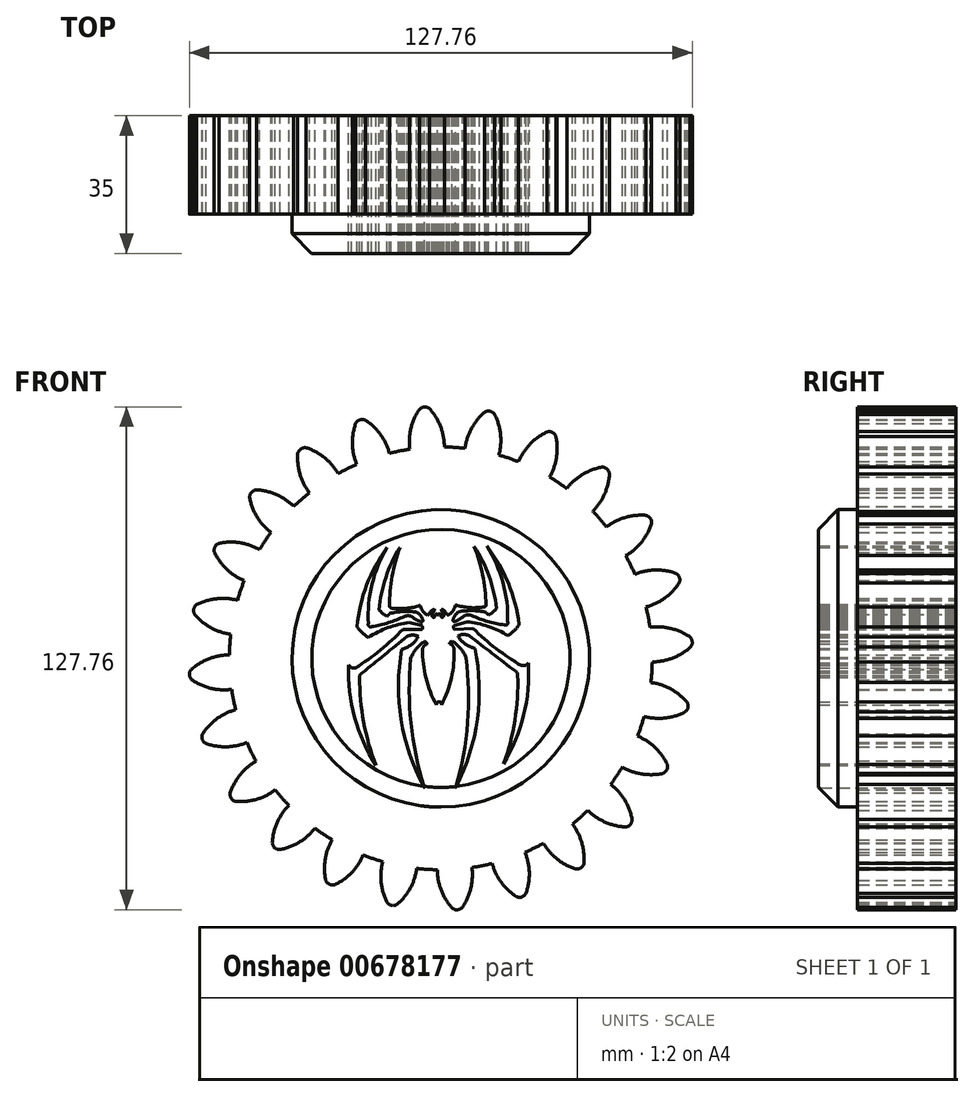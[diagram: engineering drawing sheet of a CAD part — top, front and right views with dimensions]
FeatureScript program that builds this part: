
annotation { "Feature Type Name" : "Feature", "Feature Type Description" : "" }
export const myFeature = defineFeature(function(context is Context, id is Id, definition is map)
    precondition{}
    {
        {
            var Q0;
            Q0=qCreatedBy(makeId("Front.planeOp"),FACE);
            var sketch = newSketch(context, id + "F0", { "sketchPlane" : qUnion([Q0])});
            skCircle(sketch, "E0", {"center": v(0, 0) * mm, "radius": 53.72 * mm});
            skCircle(sketch, "E1", {"center": v(0, 0) * mm, "radius": 58.67 * mm, "construction": true});
            skCircle(sketch, "E2", {"center": v(0, 0) * mm, "radius": 63.5 * mm, "construction": true});
            skLineSegment(sketch, "E3", {"start": v(0, 0) * mm, "end": v(0, 78.32) * mm, "construction": true});
            skLineSegment(sketch, "E4", {"start": v(0, 0) * mm, "end": v(-7.18, 109.5) * mm, "construction": true});
            skLineSegment(sketch, "E5", {"start": v(0, 58.67) * mm, "end": v(-85.63, 58.67) * mm, "construction": true});
            skLineSegment(sketch, "E6", {"start": v(0, 58.67) * mm, "end": v(-86.28, 27.27) * mm, "construction": true});
            skCircle(sketch, "E7", {"center": v(0, 0) * mm, "radius": 55.14 * mm, "construction": true});
            skCircle(sketch, "E8", {"center": v(0, 58.67) * mm, "radius": 14.6 * mm, "construction": true});
            skCircle(sketch, "E9", {"center": v(-13.72, 53.68) * mm, "radius": 14.6 * mm, "construction": true});
            skArc(sketch, "E10", {"start": v(0, 58.67) * mm, "mid": v(-1.2, 61.19) * mm, "end": v(-2.86, 63.44) * mm});
            skArc(sketch, "E11", {"start": v(0.88, 53.71) * mm, "mid": v(0.66, 56.23) * mm, "end": v(0, 58.67) * mm});
            skArc(sketch, "E12.MirrorCS", {"start": v(-7.88, 53.14) * mm, "mid": v(-8, 55.67) * mm, "end": v(-7.66, 58.17) * mm});
            skArc(sketch, "E13.MirrorCS", {"start": v(-7.66, 58.17) * mm, "mid": v(-6.8, 60.82) * mm, "end": v(-5.45, 63.27) * mm});
            skArc(sketch, "E14", {"start": v(-2.86, 63.44) * mm, "mid": v(-4.19, 63.88) * mm, "end": v(-5.45, 63.27) * mm});
            skArc(sketch, "E15", {"start": v(-13.64, 28.2) * mm, "mid": v(-18.83, 18.65) * mm, "end": v(-21.3, 8.08) * mm});
            skArc(sketch, "E16", {"start": v(-8.04, 9.1) * mm, "mid": v(-13.45, 7.8) * mm, "end": v(-18.43, 5.32) * mm});
            skLineSegment(sketch, "E17", {"start": v(-8.04, 9.1) * mm, "end": v(-4.86, 8.31) * mm});
            skLineSegment(sketch, "E18", {"start": v(-4.86, 7.29) * mm, "end": v(-9.63, 7.36) * mm});
            skLineSegment(sketch, "E19", {"start": v(-21.65, -2.4) * mm, "end": v(-22.74, -2.4) * mm});
            skLineSegment(sketch, "E20", {"start": v(-22.74, -2.4) * mm, "end": v(-23.41, -1.69) * mm});
            skArc(sketch, "E21", {"start": v(-23.41, -1.69) * mm, "mid": v(-21.9, -14.97) * mm, "end": v(-16.5, -27.2) * mm});
            skArc(sketch, "E22", {"start": v(-20.63, -4.83) * mm, "mid": v(-19.61, -16.2) * mm, "end": v(-16.5, -27.2) * mm});
            skArc(sketch, "E23", {"start": v(-9.94, 2.28) * mm, "mid": v(-7.48, 3.5) * mm, "end": v(-5.7, 5.59) * mm});
            skArc(sketch, "E24", {"start": v(-9.94, 2.28) * mm, "mid": v(-10.07, -15.84) * mm, "end": v(-4.14, -32.97) * mm});
            skArc(sketch, "E25", {"start": v(-7.65, 0) * mm, "mid": v(-7.58, -16.66) * mm, "end": v(-4.14, -32.97) * mm});
            skArc(sketch, "E26", {"start": v(-4.14, 4.28) * mm, "mid": v(-6.25, 2.43) * mm, "end": v(-7.65, 0) * mm});
            skArc(sketch, "E27", {"start": v(-3.56, 3.63) * mm, "mid": v(-3.72, 4.07) * mm, "end": v(-4.14, 4.28) * mm});
            skArc(sketch, "E28", {"start": v(-3.56, 3.63) * mm, "mid": v(-4.29, 3.1) * mm, "end": v(-4.65, 2.28) * mm});
            skArc(sketch, "E29", {"start": v(-4.65, 2.28) * mm, "mid": v(-3.78, -5) * mm, "end": v(-1.1, -11.85) * mm});
            skArc(sketch, "E30", {"start": v(-0.45, -11.09) * mm, "mid": v(-1, -11.27) * mm, "end": v(-1.1, -11.85) * mm});
            skArc(sketch, "E31", {"start": v(-4.86, 7.29) * mm, "mid": v(-4.65, 7.8) * mm, "end": v(-4.86, 8.31) * mm});
            skArc(sketch, "E32", {"start": v(-21.65, -2.4) * mm, "mid": v(-15.34, 2.11) * mm, "end": v(-9.63, 7.36) * mm});
            skArc(sketch, "E33", {"start": v(-5.7, 5.59) * mm, "mid": v(-7.13, 5.9) * mm, "end": v(-8.56, 5.59) * mm});
            skArc(sketch, "E34", {"start": v(-20.05, -3.75) * mm, "mid": v(-14.3, 0.92) * mm, "end": v(-8.56, 5.59) * mm});
            skArc(sketch, "E35", {"start": v(-20.05, -3.75) * mm, "mid": v(-20.51, -4.2) * mm, "end": v(-20.63, -4.83) * mm});
            skArc(sketch, "E36", {"start": v(-21.3, 8.08) * mm, "mid": v(-20.01, 6.55) * mm, "end": v(-18.43, 5.32) * mm});
            skArc(sketch, "E37", {"start": v(-13.64, 28.2) * mm, "mid": v(-17.49, 18.86) * mm, "end": v(-18.43, 8.8) * mm});
            skArc(sketch, "E38", {"start": v(-18.43, 8.8) * mm, "mid": v(-18.26, 8.16) * mm, "end": v(-17.6, 8.08) * mm});
            skArc(sketch, "E39", {"start": v(-17.6, 8.08) * mm, "mid": v(-13.31, 9.07) * mm, "end": v(-9.23, 10.69) * mm});
            skArc(sketch, "E40", {"start": v(-7.5, 10.69) * mm, "mid": v(-8.36, 10.84) * mm, "end": v(-9.23, 10.69) * mm});
            skArc(sketch, "E41", {"start": v(-7.5, 10.69) * mm, "mid": v(-6.31, 9.87) * mm, "end": v(-5.02, 9.22) * mm});
            skArc(sketch, "E42", {"start": v(-5.02, 9.22) * mm, "mid": v(-4.67, 9.36) * mm, "end": v(-4.59, 9.73) * mm});
            skArc(sketch, "E43", {"start": v(-4.59, 9.73) * mm, "mid": v(-5.14, 10.86) * mm, "end": v(-6.06, 11.72) * mm});
            skArc(sketch, "E44", {"start": v(-6.06, 11.72) * mm, "mid": v(-9.56, 11.9) * mm, "end": v(-13.03, 11.4) * mm});
            skArc(sketch, "E45", {"start": v(-13.66, 10.69) * mm, "mid": v(-13.3, 11) * mm, "end": v(-13.03, 11.4) * mm});
            skArc(sketch, "E46", {"start": v(-15.7, 12.36) * mm, "mid": v(-14.76, 11.41) * mm, "end": v(-13.66, 10.69) * mm});
            skArc(sketch, "E47", {"start": v(-10.4, 28.2) * mm, "mid": v(-14, 20.6) * mm, "end": v(-15.7, 12.36) * mm});
            skArc(sketch, "E48", {"start": v(-10.4, 28.2) * mm, "mid": v(-12.38, 20.88) * mm, "end": v(-13.03, 13.32) * mm});
            skArc(sketch, "E49", {"start": v(-13.03, 13.32) * mm, "mid": v(-12.95, 13.01) * mm, "end": v(-12.7, 12.8) * mm});
            skArc(sketch, "E50", {"start": v(-12.7, 12.8) * mm, "mid": v(-9.18, 12.67) * mm, "end": v(-5.7, 13.32) * mm});
            skArc(sketch, "E51", {"start": v(-5.2, 13.32) * mm, "mid": v(-5.46, 13.4) * mm, "end": v(-5.7, 13.32) * mm});
            skArc(sketch, "E52", {"start": v(-5.2, 13.32) * mm, "mid": v(-4.56, 11.93) * mm, "end": v(-3.36, 10.97) * mm});
            skArc(sketch, "E53", {"start": v(-3.36, 10.97) * mm, "mid": v(-3.1, 11.12) * mm, "end": v(-2.92, 11.36) * mm});
            skArc(sketch, "E54", {"start": v(-1.64, 12.5) * mm, "mid": v(-2.41, 12.08) * mm, "end": v(-2.92, 11.36) * mm});
            skArc(sketch, "E55", {"start": v(-2.1, 11.36) * mm, "mid": v(-1.8, 11.9) * mm, "end": v(-1.64, 12.5) * mm});
            skArc(sketch, "E56", {"start": v(-2.1, 11.36) * mm, "mid": v(-2.21, 11.28) * mm, "end": v(-2.25, 11.16) * mm});
            skArc(sketch, "E57", {"start": v(-2.25, 11.16) * mm, "mid": v(-2.24, 10.84) * mm, "end": v(-2.1, 10.55) * mm});
            skArc(sketch, "E58", {"start": v(-2.1, 10.55) * mm, "mid": v(-1.83, 10.41) * mm, "end": v(-1.56, 10.55) * mm});
            skArc(sketch, "E59", {"start": v(-1.1, 11.36) * mm, "mid": v(-1.44, 11.02) * mm, "end": v(-1.56, 10.55) * mm});
            skArc(sketch, "E60", {"start": v(-0.7, 10.55) * mm, "mid": v(-0.8, 11) * mm, "end": v(-1.1, 11.36) * mm});
            skArc(sketch, "E61", {"start": v(-0.7, 10.55) * mm, "mid": v(-0.52, 10.43) * mm, "end": v(-0.33, 10.36) * mm});
            skLineSegment(sketch, "E62", {"start": v(-1.1, 37.7) * mm, "end": v(-0.45, -12.72) * mm});
            skLineSegment(sketch, "E63", {"start": v(-0.45, -12.72) * mm, "end": v(-0.45, -39.14) * mm});
            skArc(sketch, "E64.MirrorCS", {"start": v(8.66, 2.52) * mm, "mid": v(9.25, -15.6) * mm, "end": v(3.77, -32.86) * mm});
            skArc(sketch, "E65.MirrorCS", {"start": v(6.43, 0.18) * mm, "mid": v(6.79, -16.48) * mm, "end": v(3.77, -32.86) * mm});
            skArc(sketch, "E66.MirrorCS", {"start": v(-0.49, -11.09) * mm, "mid": v(0.07, -11.26) * mm, "end": v(0.2, -11.83) * mm});
            skArc(sketch, "E67.MirrorCS", {"start": v(3.38, 2.39) * mm, "mid": v(2.68, -4.92) * mm, "end": v(0.2, -11.83) * mm});
            skArc(sketch, "E68.MirrorCS", {"start": v(2.24, 3.7) * mm, "mid": v(2.99, 3.2) * mm, "end": v(3.38, 2.39) * mm});
            skArc(sketch, "E69.MirrorCS", {"start": v(2.24, 3.7) * mm, "mid": v(2.4, 4.15) * mm, "end": v(2.81, 4.37) * mm});
            skArc(sketch, "E70.MirrorCS", {"start": v(2.81, 4.37) * mm, "mid": v(4.96, 2.57) * mm, "end": v(6.43, 0.18) * mm});
            skArc(sketch, "E71.MirrorCS", {"start": v(8.66, 2.52) * mm, "mid": v(6.17, 3.67) * mm, "end": v(4.34, 5.72) * mm});
            skArc(sketch, "E72.MirrorCS", {"start": v(4.34, 5.72) * mm, "mid": v(5.76, 6.07) * mm, "end": v(7.2, 5.8) * mm});
            skArc(sketch, "E73.MirrorCS", {"start": v(18.92, -3.25) * mm, "mid": v(13.05, 1.27) * mm, "end": v(7.2, 5.8) * mm});
            skArc(sketch, "E74.MirrorCS", {"start": v(20.48, -1.86) * mm, "mid": v(14.06, 2.49) * mm, "end": v(8.22, 7.59) * mm});
            skArc(sketch, "E75.MirrorCS", {"start": v(22.23, -1.1) * mm, "mid": v(21.06, -14.42) * mm, "end": v(15.98, -26.78) * mm});
            skArc(sketch, "E76.MirrorCS", {"start": v(19.53, -4.32) * mm, "mid": v(18.8, -15.71) * mm, "end": v(15.98, -26.78) * mm});
            skArc(sketch, "E77.MirrorCS", {"start": v(18.92, -3.25) * mm, "mid": v(19.4, -3.68) * mm, "end": v(19.53, -4.32) * mm});
            skLineSegment(sketch, "E78.MirrorCS", {"start": v(20.48, -1.86) * mm, "end": v(21.58, -1.83) * mm});
            skLineSegment(sketch, "E79.MirrorCS", {"start": v(21.58, -1.83) * mm, "end": v(22.23, -1.1) * mm});
            skLineSegment(sketch, "E80.MirrorCS", {"start": v(3.45, 7.4) * mm, "end": v(8.22, 7.59) * mm});
            skArc(sketch, "E81.MirrorCS", {"start": v(3.45, 7.4) * mm, "mid": v(3.23, 7.9) * mm, "end": v(3.42, 8.42) * mm});
            skLineSegment(sketch, "E82.MirrorCS", {"start": v(6.58, 9.28) * mm, "end": v(3.42, 8.42) * mm});
            skArc(sketch, "E83.MirrorCS", {"start": v(6.58, 9.28) * mm, "mid": v(12.03, 8.12) * mm, "end": v(17.07, 5.78) * mm});
            skArc(sketch, "E84.MirrorCS", {"start": v(16.16, 8.5) * mm, "mid": v(11.86, 9.39) * mm, "end": v(7.74, 10.9) * mm});
            skArc(sketch, "E85.MirrorCS", {"start": v(6, 10.86) * mm, "mid": v(6.86, 11.04) * mm, "end": v(7.74, 10.9) * mm});
            skArc(sketch, "E86.MirrorCS", {"start": v(6, 10.86) * mm, "mid": v(4.84, 10) * mm, "end": v(3.56, 9.33) * mm});
            skArc(sketch, "E87.MirrorCS", {"start": v(3.56, 9.33) * mm, "mid": v(3.2, 9.46) * mm, "end": v(3.12, 9.83) * mm});
            skArc(sketch, "E88.MirrorCS", {"start": v(19.87, 8.6) * mm, "mid": v(18.62, 7.04) * mm, "end": v(17.07, 5.78) * mm});
            skArc(sketch, "E89.MirrorCS", {"start": v(11.7, 28.52) * mm, "mid": v(17.13, 19.11) * mm, "end": v(19.87, 8.6) * mm});
            skArc(sketch, "E90.MirrorCS", {"start": v(11.7, 28.52) * mm, "mid": v(15.78, 19.29) * mm, "end": v(16.98, 9.26) * mm});
            skArc(sketch, "E91.MirrorCS", {"start": v(14.15, 12.74) * mm, "mid": v(13.25, 11.77) * mm, "end": v(12.16, 11.02) * mm});
            skArc(sketch, "E92.MirrorCS", {"start": v(4.54, 11.85) * mm, "mid": v(8.03, 12.13) * mm, "end": v(11.51, 11.71) * mm});
            skArc(sketch, "E93.MirrorCS", {"start": v(12.16, 11.02) * mm, "mid": v(11.8, 11.33) * mm, "end": v(11.51, 11.71) * mm});
            skArc(sketch, "E94.MirrorCS", {"start": v(3.12, 9.83) * mm, "mid": v(3.64, 10.97) * mm, "end": v(4.54, 11.85) * mm});
            skArc(sketch, "E95.MirrorCS", {"start": v(3.64, 13.44) * mm, "mid": v(3.03, 12.02) * mm, "end": v(1.86, 11.03) * mm});
            skArc(sketch, "E96.MirrorCS", {"start": v(11.16, 13.1) * mm, "mid": v(7.63, 12.88) * mm, "end": v(4.15, 13.45) * mm});
            skArc(sketch, "E97.MirrorCS", {"start": v(3.64, 13.44) * mm, "mid": v(3.9, 13.52) * mm, "end": v(4.15, 13.45) * mm});
            skArc(sketch, "E98.MirrorCS", {"start": v(8.46, 28.44) * mm, "mid": v(10.63, 21.17) * mm, "end": v(11.46, 13.64) * mm});
            skArc(sketch, "E99.MirrorCS", {"start": v(8.46, 28.44) * mm, "mid": v(12.24, 20.93) * mm, "end": v(14.15, 12.74) * mm});
            skArc(sketch, "E100.MirrorCS", {"start": v(0.1, 12.52) * mm, "mid": v(0.88, 12.12) * mm, "end": v(1.4, 11.42) * mm});
            skArc(sketch, "E101.MirrorCS", {"start": v(0.59, 11.4) * mm, "mid": v(0.27, 11.93) * mm, "end": v(0.1, 12.52) * mm});
            skArc(sketch, "E102.MirrorCS", {"start": v(-0.42, 11.37) * mm, "mid": v(-0.06, 11.04) * mm, "end": v(0.07, 10.57) * mm});
            skArc(sketch, "E103.MirrorCS", {"start": v(-0.8, 10.55) * mm, "mid": v(-0.7, 11) * mm, "end": v(-0.42, 11.37) * mm});
            skArc(sketch, "E104.MirrorCS", {"start": v(-0.8, 10.55) * mm, "mid": v(-0.96, 10.43) * mm, "end": v(-1.15, 10.34) * mm});
            skArc(sketch, "E105.MirrorCS", {"start": v(0.6, 10.59) * mm, "mid": v(0.34, 10.44) * mm, "end": v(0.07, 10.57) * mm});
            skArc(sketch, "E106.MirrorCS", {"start": v(1.86, 11.03) * mm, "mid": v(1.6, 11.18) * mm, "end": v(1.4, 11.42) * mm});
            skArc(sketch, "E107.MirrorCS", {"start": v(0.59, 11.4) * mm, "mid": v(0.7, 11.32) * mm, "end": v(0.75, 11.2) * mm});
            skArc(sketch, "E108.MirrorCS", {"start": v(0.75, 11.2) * mm, "mid": v(0.74, 10.88) * mm, "end": v(0.6, 10.59) * mm});
            skArc(sketch, "E109.MirrorCS", {"start": v(11.46, 13.64) * mm, "mid": v(11.4, 13.32) * mm, "end": v(11.16, 13.1) * mm});
            skArc(sketch, "E110.MirrorCS", {"start": v(16.98, 9.26) * mm, "mid": v(16.83, 8.6) * mm, "end": v(16.16, 8.5) * mm});
            skCircle(sketch, "E111", {"center": v(0, 0) * mm, "radius": 37.8 * mm});
            skSolve(sketch);
        }
        {
            var Q0;
            Q0=makeQuery(id+"F0.imprint","IMPRINT",FACE,{"disambiguationData":[TD([[makeQuery(id+"F0.imprint","IMPRINT",EDGE,{"derivedFrom":sQuery(id+"F0.wireOp",EDGE,"E111")}),-1.0]])]});
            var Q1;
            Q1=makeQuery(id+"F0.imprint","IMPRINT",FACE,{"disambiguationData":[TD([[makeQuery(id+"F0.imprint","IMPRINT",EDGE,{"derivedFrom":sQuery(id+"F0.wireOp",EDGE,"E10")}),1.0]])]});
            extrude(context, id + "F1", {"entities" : qUnion([Q0, Q1]), "depth" : 25 * mm, "offsetDistance" : 25 * mm});
        }
        {
            var Q0;
            Q0=makeQuery(id+"F1.opExtrude","SWEPT_BODY",BODY,{"disambiguationData":[OSD([sQuery(id+"F0.wireOp",EDGE,"E0"),sQuery(id+"F0.wireOp",EDGE,"E10"),sQuery(id+"F0.wireOp",EDGE,"E11"),sQuery(id+"F0.wireOp",EDGE,"E12.MirrorCS"),sQuery(id+"F0.wireOp",EDGE,"E13.MirrorCS"),sQuery(id+"F0.wireOp",EDGE,"E14")])]});
            var Q1;
            Q1=makeQuery(id+"F1.opExtrude","SWEPT_FACE",FACE,{"disambiguationData":[OSD([sQuery(id+"F0.wireOp",EDGE,"E0")])]});
            circularPattern(context, id + "F2", {"entities" : qUnion([Q0]), "axis" : qUnion([Q1]), "angle" : 360 * degree, "instanceCount" : 24, "equalSpace" : true});
        }
        {
            var Q0;
            Q0=makeQuery(id+"F0.imprint","IMPRINT",FACE,{"disambiguationData":[TD([[makeQuery(id+"F0.imprint","IMPRINT",EDGE,{"derivedFrom":sQuery(id+"F0.wireOp",EDGE,"E15")}),-1.0]])]});
            extrude(context, id + "F3", {"entities" : qUnion([Q0]), "operationType" : NewBodyOperationType.ADD, "depth" : 35 * mm, "offsetDistance" : 25 * mm});
        }
        {
            var Q0;
            Q0=makeQuery(id+"F3.opExtrude","CAP_EDGE",EDGE,{"disambiguationData":[OSD([sQuery(id+"F0.wireOp",EDGE,"E111")])],"isStart":false});
            chamfer(context, id + "F4", {"entities" : qUnion([Q0]), "width" : 5 * mm, "tangentPropagation" : true});
        }
    });
